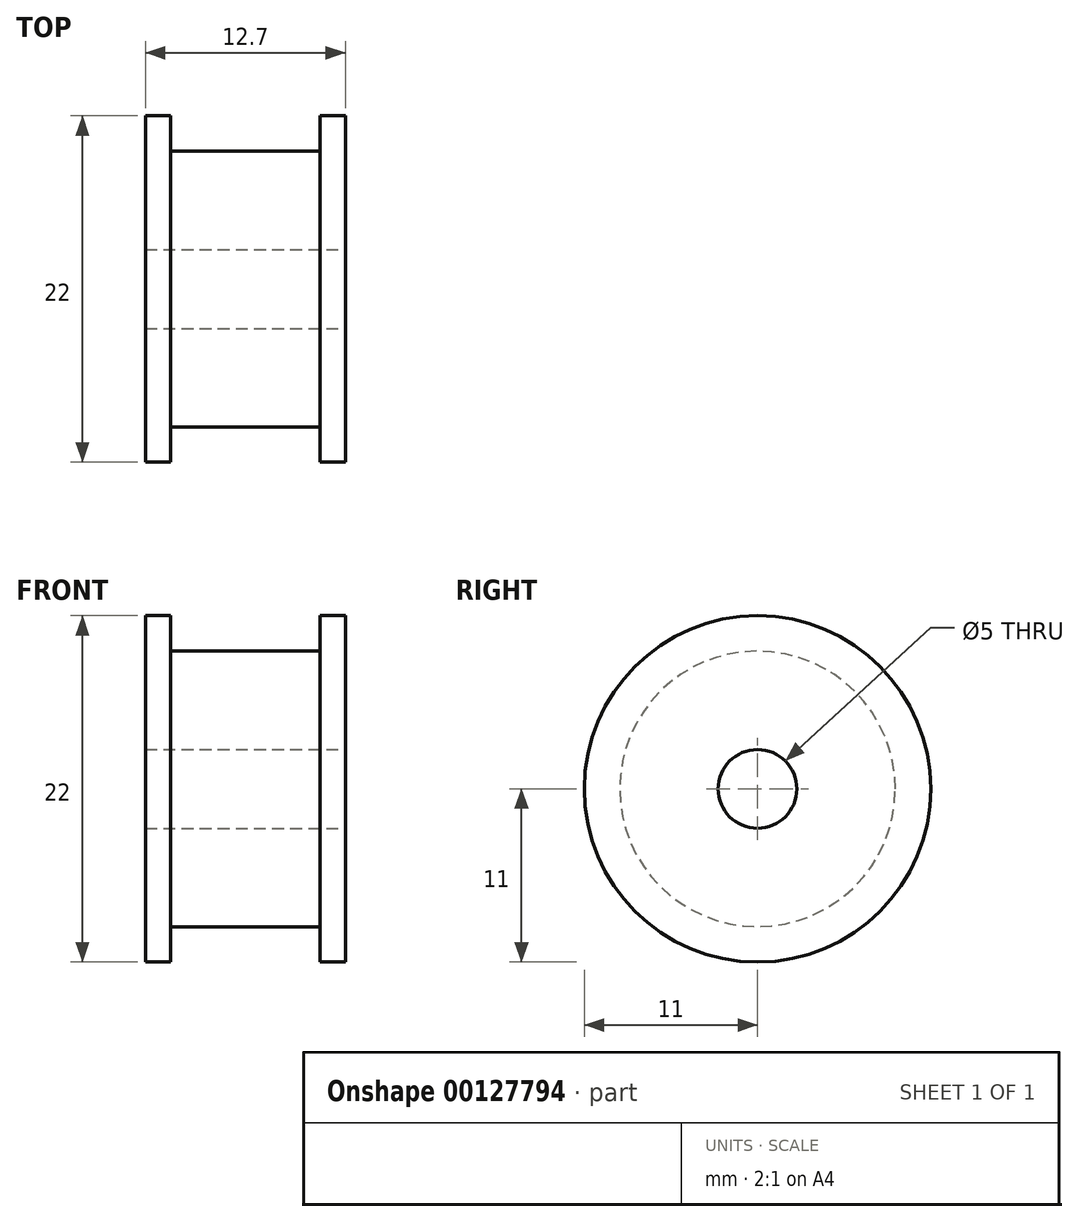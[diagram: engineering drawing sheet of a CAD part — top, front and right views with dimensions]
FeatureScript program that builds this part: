
annotation { "Feature Type Name" : "Feature", "Feature Type Description" : "" }
export const myFeature = defineFeature(function(context is Context, id is Id, definition is map)
    precondition{}
    {
        {
            var Q0;
            Q0=qCreatedBy(makeId("Front.planeOp"),FACE);
            var sketch = newSketch(context, id + "F0", { "sketchPlane" : qUnion([Q0])});
            skLineSegment(sketch, "E0", {"start": v(-6.35, 0) * mm, "end": v(6.35, 0) * mm});
            skLineSegment(sketch, "E1", {"start": v(-6.35, 0) * mm, "end": v(-6.35, 11) * mm});
            skLineSegment(sketch, "E2", {"start": v(-6.35, 11) * mm, "end": v(-4.75, 11) * mm});
            skLineSegment(sketch, "E3", {"start": v(-4.75, 11) * mm, "end": v(-4.75, 8.75) * mm});
            skLineSegment(sketch, "E4", {"start": v(-4.75, 8.75) * mm, "end": v(4.75, 8.75) * mm});
            skLineSegment(sketch, "E5", {"start": v(4.75, 8.75) * mm, "end": v(4.75, 11) * mm});
            skLineSegment(sketch, "E6", {"start": v(4.75, 11) * mm, "end": v(6.35, 11) * mm});
            skLineSegment(sketch, "E7", {"start": v(6.35, 11) * mm, "end": v(6.35, 0) * mm});
            skLineSegment(sketch, "E8", {"start": v(-25.73, 0) * mm, "end": v(0, 0) * mm, "construction": true});
            skLineSegment(sketch, "E9", {"start": v(0, 0) * mm, "end": v(0, 45) * mm, "construction": true});
            skSolve(sketch);
        }
        {
            var Q0;
            Q0=makeQuery(id+"F0.imprint","IMPRINT",FACE,{"disambiguationData":[TD([[makeQuery(id+"F0.imprint","IMPRINT",EDGE,{"derivedFrom":sQuery(id+"F0.wireOp",EDGE,"E0")}),1.0]])]});
            var Q1;
            Q1=sQuery(id+"F0.wireOp",EDGE,"E8");
            revolve(context, id + "F1", {"entities" : qUnion([Q0]), "axis" : qUnion([Q1]), "revolveType" : RevolveType.FULL});
        }
        {
            var Q0;
            Q0=makeQuery(id+"F1.opRevolve","SWEPT_FACE",FACE,{"disambiguationData":[OSD([sQuery(id+"F0.wireOp",EDGE,"E7")])]});
            var sketch = newSketch(context, id + "F2", { "sketchPlane" : qUnion([Q0])});
            skCircle(sketch, "E10", {"center": v(0, 0) * mm, "radius": 2.5 * mm});
            skSolve(sketch);
        }
        {
            var Q0;
            Q0 = qSketchRegion(id + "F2", true);
            extrude(context, id + "F3", {"entities" : qUnion([Q0]), "operationType" : NewBodyOperationType.REMOVE, "endBound" : BoundingType.THROUGH_ALL, "oppositeDirection" : true, "depth" : 25 * mm});
        }
    });
